# Revit family: 418B-W-RD
name_source: partatom
category: Plumbing Fixtures
revit_build: Autodesk Revit MEP 2016 (Build: 20150220_1215(x64)
units: mm (PartAtom-declared; Revit-internal decimal feet)

## family parameters
Cut with Voids When Loaded = No
Host = Face
OmniClass Number = 23.45.05.14.17
OmniClass Title = Showers
Part Type = Normal
Room Calculation Point = No
Round Connector Dimension = Use Diameter
Shared = Yes

## types (1)
- 418B-W-RD
    -0 Electronic Valves, Single-Temp Metering (Specify Type Where Indicated) = No
    -1 Flo-Cloz, H & C = Yes
    -5 Flo-Cloz, Single Temperature = No
    -6 Air-Control, Single Temperature Metering = No
    -7 Meter-Matic, Single Temperature Metering = No
    -8 T/P Temperature-Pressure Balancing Mixing Valve With Patented Ligature Resistant Tri-Lever Handle (ASSE1016 Compliant) = Yes
    -9 Without Valves (Valves by Others) = No
    -BS - Built-in Liquid Soap System = No
    -CSH Conical Showerhead (Ligature Resistant) = No
    -D - Soap Dish = No
    -EG Enviro-Glaze (Specify Color) = No
    -EVS1 Electronic Valve System - Single Temp = No
    -EVSP1 Electronic Valve Sys. w/ Piezo Pushbutton = No
    -F - Flow Control, Must Specify: 1.4 GPM, 1.6 GPM, 2.0 GPM = No
    -FG - 14 Gage Panel = No
    -FX Hand Shower With 60" Stainless Steel Hose (In Lieu of Conventional Showerhead) -QD Quick-Disconnect, -PSO -QD w/ Positive Shut-Off = No
    -G Individual Stops (Flo-Cloz Only) = No
    -H Hand Volume Control = No
    -K Allen Key Volume Control = No
    -LVR Lever Handle (-5 & 8 Valves) = No
    -MS Modular Privacy Compartments (See Diana Privacy Tab) = No
    -MSH Multi-Stream Shower Head = No
    -MV Metering Valve in Riser (Air-Control) = No
    -MVC1 Time-Trol - Single Temp, Specify Options: -CI Cycle Interrupt = No
    -P Penal Shower Head = No
    -PBH Hemispherical Pushbutton = No
    -PPZ1 - Programmable Piezo Pushbutton (Single Temperature Only) = No
    -RD Recessed Soap Dish = Yes
    -SB 24" Slide Bar (For -FX Hand Shower) = No
    -TF Transformer = No
    -W Wall = Yes
    -WS Without Showerhead Without Shower Head Punching, Unless Otherwise Specified = No
    -Y Universal Ball Joint = No
    -YY Lockable Universal Ball Joint = No
    -Z Up-Down Ball Joint = No
    -ZZ Lockable Up-Down Ball Joint = No
    4 - Apex = Yes
    Assembly Code = D2010710
    CW Connection = Yes
    CWFU = 2
    Default Elevation = 72"
    Description = Acorn Shower-Ware® 410B Series Apex Type 1 Flush-Mounted Shower
    HW Connection = Yes
    HWFU = 3
    Manufacturer = Acorn Engineering Company
    Material = Stainless Steel-Acorn-Type 304-Satin
    Model = 418B-W-RD
    Revised Date = 09/21/2015
    URL = http://www.acorneng.com
    Vent Connection = No
    WFU = 4
    Waste Connection = No

## geometry (parser evidence)
native form markers: Sweep x3
no freeform markers — native parametric forms only
